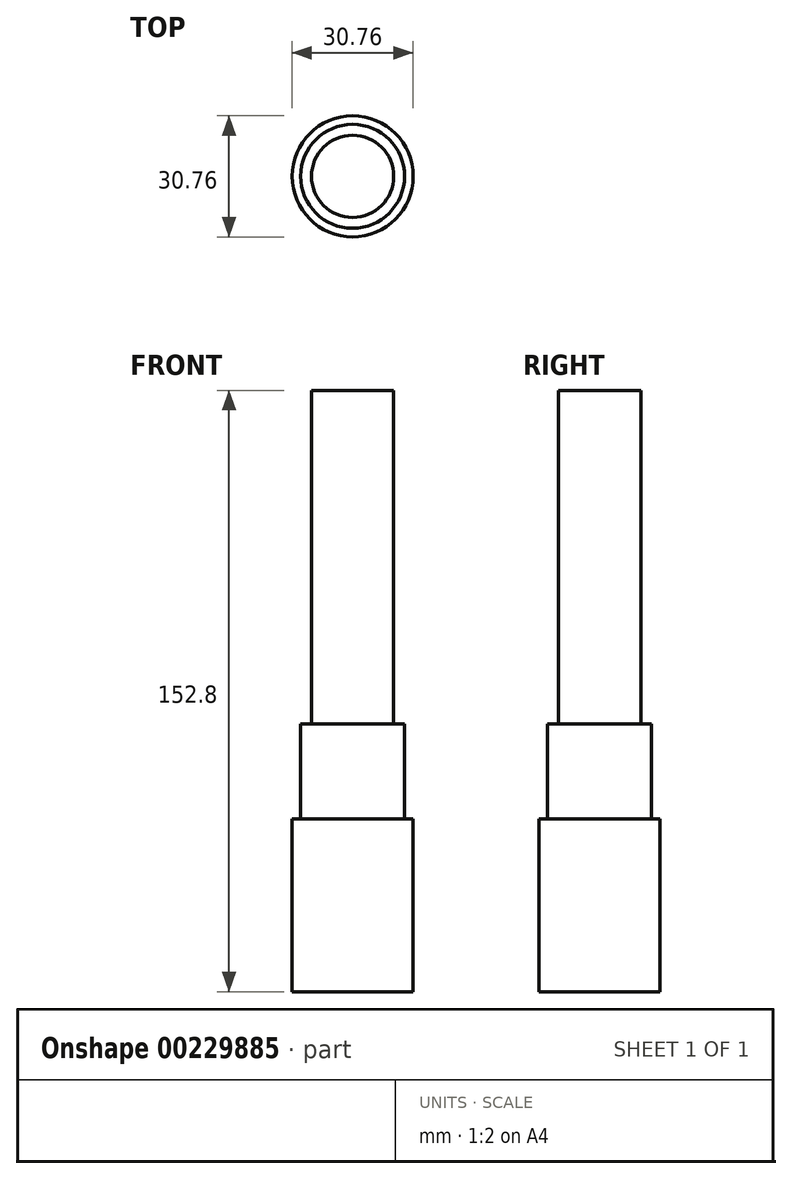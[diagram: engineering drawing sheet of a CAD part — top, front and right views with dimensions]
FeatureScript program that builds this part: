
annotation { "Feature Type Name" : "Feature", "Feature Type Description" : "" }
export const myFeature = defineFeature(function(context is Context, id is Id, definition is map)
    precondition{}
    {
        {
            var Q0;
            Q0=qCreatedBy(makeId("Top.planeOp"),FACE);
            var sketch = newSketch(context, id + "F0", { "sketchPlane" : qUnion([Q0])});
            skCircle(sketch, "E0", {"center": v(0, 0) * mm, "radius": 15.38 * mm});
            skCircle(sketch, "E1", {"center": v(0, 0) * mm, "radius": 13.2 * mm});
            skCircle(sketch, "E2", {"center": v(0, 0) * mm, "radius": 10.45 * mm});
            skSolve(sketch);
        }
        {
            var Q0;
            Q0 = qSketchRegion(id + "F0", true);
            extrude(context, id + "F1", {"entities" : qUnion([Q0]), "depth" : 43.96 * mm});
        }
        {
            var Q0;
            Q0=makeQuery(id+"F0.imprint","IMPRINT",FACE,{"disambiguationData":[TD([[makeQuery(id+"F0.imprint","IMPRINT",EDGE,{"derivedFrom":sQuery(id+"F0.wireOp",EDGE,"E1")}),1.0]])]});
            extrude(context, id + "F3", {"entities" : qUnion([Q0]), "operationType" : NewBodyOperationType.ADD, "depth" : 68 * mm});
        }
        {
            var Q0;
            Q0=makeQuery(id+"F0.imprint","IMPRINT",FACE,{"disambiguationData":[TD([[makeQuery(id+"F0.imprint","IMPRINT",EDGE,{"derivedFrom":sQuery(id+"F0.wireOp",EDGE,"E2")}),1.0]])]});
            extrude(context, id + "F2", {"entities" : qUnion([Q0]), "operationType" : NewBodyOperationType.ADD, "depth" : 152.8 * mm});
        }
    });
